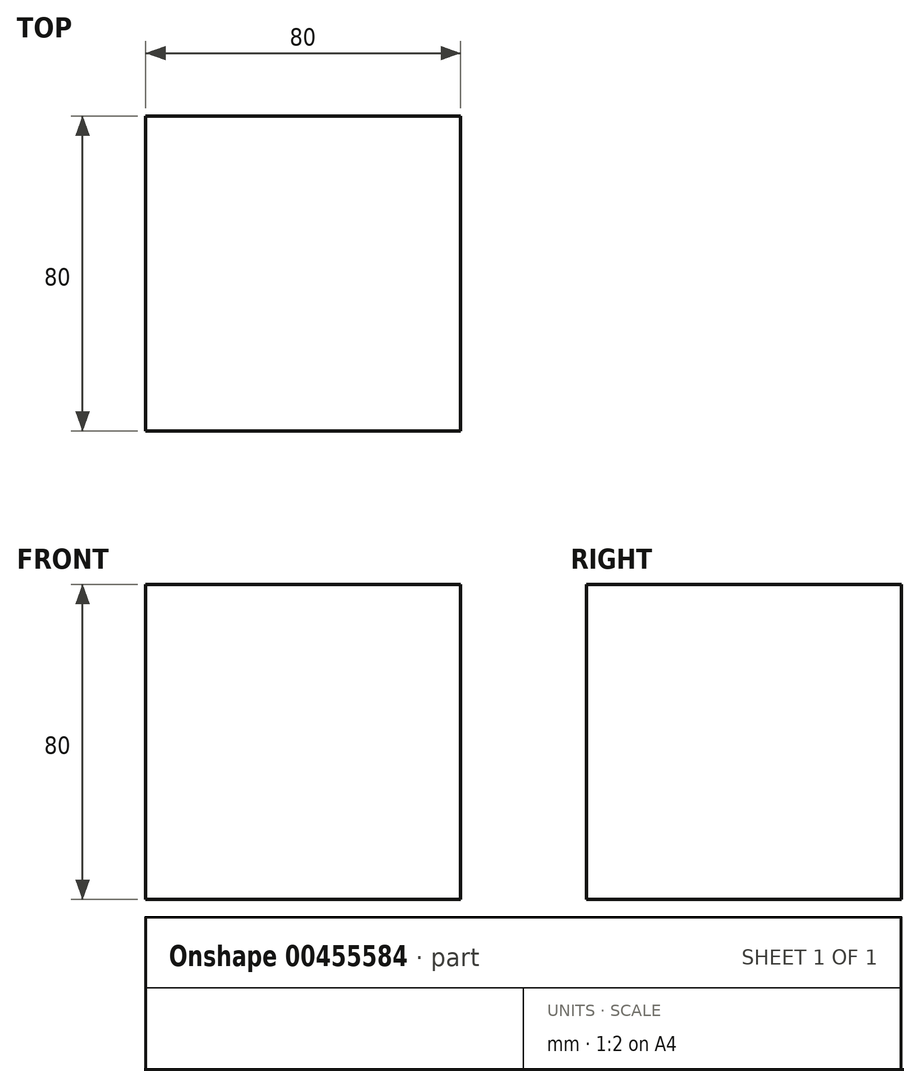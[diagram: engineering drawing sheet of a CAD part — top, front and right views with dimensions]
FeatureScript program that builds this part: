
annotation { "Feature Type Name" : "Feature", "Feature Type Description" : "" }
export const myFeature = defineFeature(function(context is Context, id is Id, definition is map)
    precondition{}
    {
        {
            var Q0;
            Q0=qCreatedBy(makeId("Top.planeOp"),FACE);
            var sketch = newSketch(context, id + "F0", { "sketchPlane" : qUnion([Q0])});
            skLineSegment(sketch, "E0.bottom", {"start": v(-40, 40) * mm, "end": v(40, 40) * mm});
            skLineSegment(sketch, "E0.top", {"start": v(-40, -40) * mm, "end": v(40, -40) * mm});
            skLineSegment(sketch, "E0.left", {"start": v(-40, 40) * mm, "end": v(-40, -40) * mm});
            skLineSegment(sketch, "E0.right", {"start": v(40, 40) * mm, "end": v(40, -40) * mm});
            skSolve(sketch);
        }
        {
            var Q0;
            Q0=makeQuery(id+"F0.imprint","IMPRINT",FACE,{"disambiguationData":[TD([[makeQuery(id+"F0.imprint","IMPRINT",EDGE,{"derivedFrom":sQuery(id+"F0.wireOp",EDGE,"E0.bottom")}),-1.0]])]});
            extrude(context, id + "F1", {"entities" : qUnion([Q0]), "depth" : 80 * mm});
        }
    });
